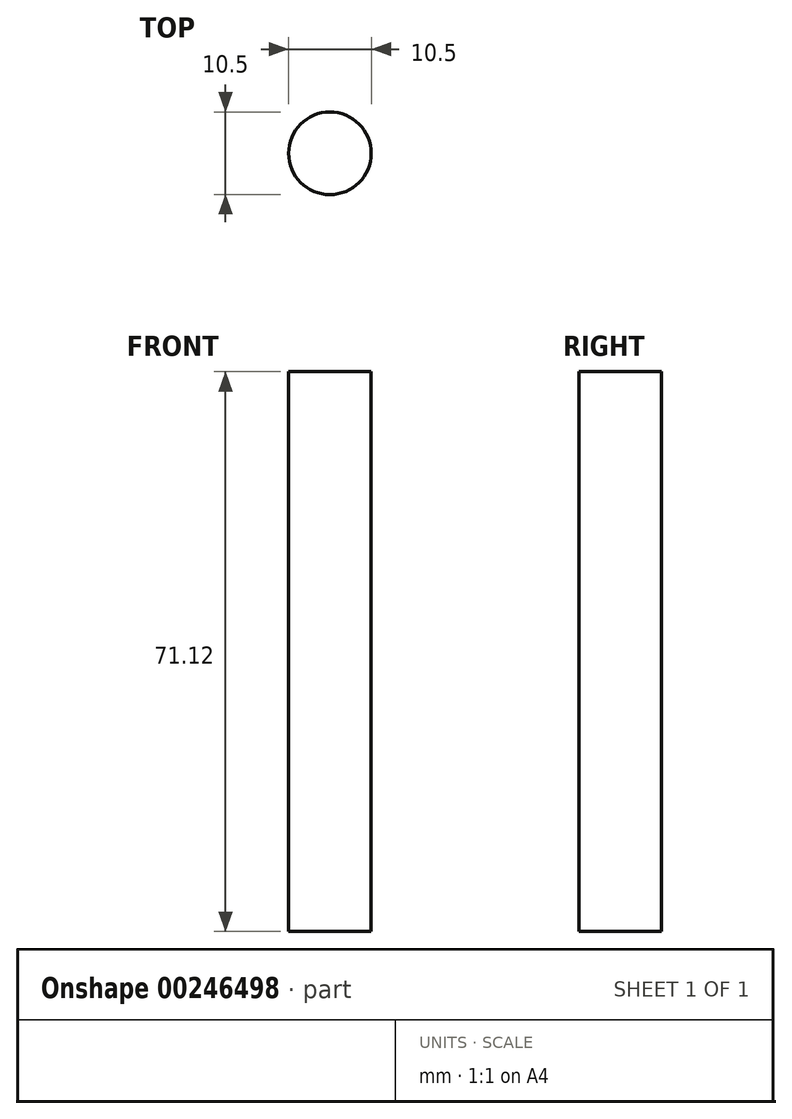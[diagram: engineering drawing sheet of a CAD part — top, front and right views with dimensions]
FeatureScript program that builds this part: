
annotation { "Feature Type Name" : "Feature", "Feature Type Description" : "" }
export const myFeature = defineFeature(function(context is Context, id is Id, definition is map)
    precondition{}
    {
        {
            var Q0;
            Q0=qCreatedBy(makeId("Top.planeOp"),FACE);
            var sketch = newSketch(context, id + "F0", { "sketchPlane" : qUnion([Q0])});
            skCircle(sketch, "E0", {"center": v(0, 0) * mm, "radius": 5.25 * mm});
            skSolve(sketch);
        }
        {
            var Q0;
            Q0 = qSketchRegion(id + "F0", true);
            extrude(context, id + "F1", {"entities" : qUnion([Q0]), "depth" : 71.12 * mm});
        }
    });
